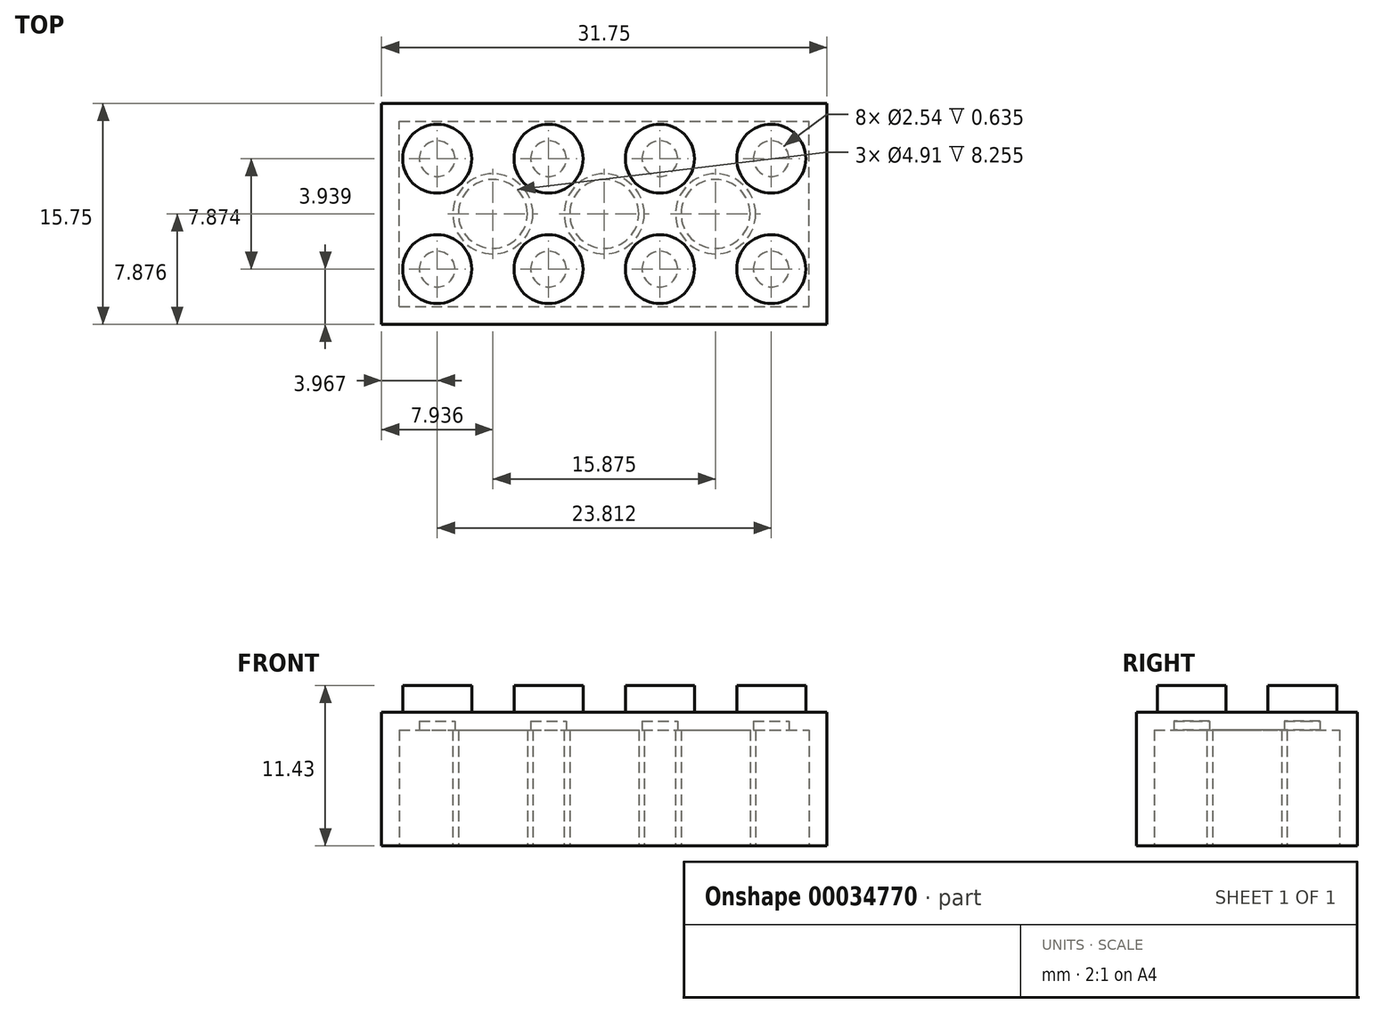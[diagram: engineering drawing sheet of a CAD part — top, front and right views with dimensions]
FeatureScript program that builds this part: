
annotation { "Feature Type Name" : "Feature", "Feature Type Description" : "" }
export const myFeature = defineFeature(function(context is Context, id is Id, definition is map)
    precondition{}
    {
        {
            var Q0;
            Q0=qCreatedBy(makeId("Front.planeOp"),FACE);
            var sketch = newSketch(context, id + "F0", { "sketchPlane" : qUnion([Q0])});
            skLineSegment(sketch, "E0.bottom", {"start": v(-17.81, 25.4) * mm, "end": v(13.94, 25.4) * mm});
            skLineSegment(sketch, "E0.top", {"start": v(-17.81, 13.96) * mm, "end": v(13.94, 13.96) * mm});
            skLineSegment(sketch, "E0.left", {"start": v(-17.81, 25.4) * mm, "end": v(-17.81, 13.96) * mm});
            skLineSegment(sketch, "E0.right", {"start": v(13.94, 25.4) * mm, "end": v(13.94, 13.96) * mm});
            skSolve(sketch);
        }
        {
            var Q0;
            Q0=makeQuery(id+"F0.imprint","IMPRINT",FACE,{"disambiguationData":[TD([[makeQuery(id+"F0.imprint","IMPRINT",EDGE,{"derivedFrom":sQuery(id+"F0.wireOp",EDGE,"E0.bottom")}),-1.0]])]});
            extrude(context, id + "F1", {"entities" : qUnion([Q0]), "depth" : 15.75 * mm});
        }
        {
            var Q0;
            Q0=makeQuery(id+"F1.opExtrude","SWEPT_FACE",FACE,{"disambiguationData":[OSD([sQuery(id+"F0.wireOp",EDGE,"E0.bottom")])]});
            var sketch = newSketch(context, id + "F2", { "sketchPlane" : qUnion([Q0])});
            skCircle(sketch, "E1", {"center": v(9.97, -11.81) * mm, "radius": 2.46 * mm});
            skCircle(sketch, "E2", {"center": v(2.03, -11.81) * mm, "radius": 2.46 * mm});
            skCircle(sketch, "E3", {"center": v(9.97, -3.94) * mm, "radius": 2.46 * mm});
            skCircle(sketch, "E4", {"center": v(2.03, -3.94) * mm, "radius": 2.46 * mm});
            skCircle(sketch, "E5", {"center": v(-5.9, -3.94) * mm, "radius": 2.46 * mm});
            skCircle(sketch, "E6", {"center": v(-5.9, -11.81) * mm, "radius": 2.46 * mm});
            skCircle(sketch, "E7", {"center": v(-13.84, -3.94) * mm, "radius": 2.46 * mm});
            skPoint(sketch, "E7.perimeterSnap0", {"position": v(-13.84, -3.94) * mm});
            skCircle(sketch, "E8", {"center": v(-13.84, -11.81) * mm, "radius": 2.46 * mm});
            skSolve(sketch);
        }
        {
            var Q0;
            Q0=makeQuery(id+"F2.imprint","IMPRINT",FACE,{"disambiguationData":[TD([[makeQuery(id+"F2.imprint","IMPRINT",EDGE,{"derivedFrom":sQuery(id+"F2.wireOp",EDGE,"E1")}),-1.0]])]});
            extrude(context, id + "F3", {"entities" : qUnion([Q0]), "operationType" : NewBodyOperationType.REMOVE, "oppositeDirection" : true, "depth" : 1.9 * mm});
        }
        {
            var Q0;
            Q0=makeQuery(id+"F1.opExtrude","SWEPT_FACE",FACE,{"disambiguationData":[OSD([sQuery(id+"F0.wireOp",EDGE,"E0.top")])]});
            var sketch = newSketch(context, id + "F4", { "sketchPlane" : qUnion([Q0])});
            skCircle(sketch, "E9", {"center": v(-13.84, 11.81) * mm, "radius": 1.27 * mm});
            skCircle(sketch, "E10", {"center": v(-13.84, 3.94) * mm, "radius": 1.27 * mm});
            skCircle(sketch, "E11", {"center": v(-5.9, 3.94) * mm, "radius": 1.27 * mm});
            skCircle(sketch, "E12", {"center": v(2.03, 3.94) * mm, "radius": 1.27 * mm});
            skCircle(sketch, "E13", {"center": v(9.97, 3.94) * mm, "radius": 1.27 * mm});
            skCircle(sketch, "E14", {"center": v(9.97, 11.81) * mm, "radius": 1.27 * mm});
            skCircle(sketch, "E15", {"center": v(2.03, 11.81) * mm, "radius": 1.27 * mm});
            skCircle(sketch, "E16", {"center": v(-5.9, 11.81) * mm, "radius": 1.27 * mm});
            skLineSegment(sketch, "E17.0", {"start": v(-16.54, 1.27) * mm, "end": v(12.67, 1.27) * mm});
            skLineSegment(sketch, "E17.1", {"start": v(-16.54, 14.48) * mm, "end": v(-16.54, 1.27) * mm});
            skLineSegment(sketch, "E17.2", {"start": v(-16.54, 14.48) * mm, "end": v(12.67, 14.48) * mm});
            skLineSegment(sketch, "E17.3", {"start": v(12.67, 14.48) * mm, "end": v(12.67, 1.27) * mm});
            skLineSegment(sketch, "E18", {"start": v(9.97, 3.94) * mm, "end": v(9.97, 11.81) * mm});
            skLineSegment(sketch, "E19", {"start": v(2.03, 11.81) * mm, "end": v(2.03, 3.94) * mm});
            skLineSegment(sketch, "E20", {"start": v(-5.9, 3.94) * mm, "end": v(-5.9, 11.81) * mm});
            skLineSegment(sketch, "E21", {"start": v(-13.84, 11.81) * mm, "end": v(-13.84, 3.94) * mm});
            skLineSegment(sketch, "E22", {"start": v(-13.84, 7.87) * mm, "end": v(-5.9, 7.87) * mm});
            skLineSegment(sketch, "E23", {"start": v(-5.9, 7.87) * mm, "end": v(2.03, 7.87) * mm});
            skLineSegment(sketch, "E24", {"start": v(2.03, 7.87) * mm, "end": v(9.97, 7.87) * mm});
            skCircle(sketch, "E25", {"center": v(6, 7.87) * mm, "radius": 2.86 * mm});
            skCircle(sketch, "E26", {"center": v(-1.94, 7.87) * mm, "radius": 2.86 * mm});
            skCircle(sketch, "E27", {"center": v(-9.87, 7.87) * mm, "radius": 2.86 * mm});
            skCircle(sketch, "E28", {"center": v(6, 7.87) * mm, "radius": 2.46 * mm});
            skCircle(sketch, "E29", {"center": v(-1.94, 7.87) * mm, "radius": 2.46 * mm});
            skCircle(sketch, "E30", {"center": v(-9.87, 7.87) * mm, "radius": 2.46 * mm});
            skSolve(sketch);
        }
        {
            var Q0;
            Q0=makeQuery(id+"F4.imprint","IMPRINT",FACE,{"disambiguationData":[TD([[makeQuery(id+"F4.imprint","IMPRINT",EDGE,{"derivedFrom":sQuery(id+"F4.wireOp",EDGE,"E13")}),1.0]])]});
            var Q1;
            Q1=makeQuery(id+"F4.imprint","IMPRINT",FACE,{"disambiguationData":[TD([[makeQuery(id+"F4.imprint","IMPRINT",EDGE,{"derivedFrom":sQuery(id+"F4.wireOp",EDGE,"E14")}),1.0]])]});
            var Q2;
            Q2=makeQuery(id+"F4.imprint","IMPRINT",FACE,{"disambiguationData":[TD([[makeQuery(id+"F4.imprint","IMPRINT",EDGE,{"derivedFrom":sQuery(id+"F4.wireOp",EDGE,"E15")}),1.0]])]});
            var Q3;
            Q3=makeQuery(id+"F4.imprint","IMPRINT",FACE,{"disambiguationData":[TD([[makeQuery(id+"F4.imprint","IMPRINT",EDGE,{"derivedFrom":sQuery(id+"F4.wireOp",EDGE,"E12")}),1.0]])]});
            var Q4;
            Q4=makeQuery(id+"F4.imprint","IMPRINT",FACE,{"disambiguationData":[TD([[makeQuery(id+"F4.imprint","IMPRINT",EDGE,{"derivedFrom":sQuery(id+"F4.wireOp",EDGE,"E16")}),1.0]])]});
            var Q5;
            Q5=makeQuery(id+"F4.imprint","IMPRINT",FACE,{"disambiguationData":[TD([[makeQuery(id+"F4.imprint","IMPRINT",EDGE,{"derivedFrom":sQuery(id+"F4.wireOp",EDGE,"E11")}),1.0]])]});
            var Q6;
            Q6=makeQuery(id+"F4.imprint","IMPRINT",FACE,{"disambiguationData":[TD([[makeQuery(id+"F4.imprint","IMPRINT",EDGE,{"derivedFrom":sQuery(id+"F4.wireOp",EDGE,"E9")}),1.0]])]});
            var Q7;
            Q7=makeQuery(id+"F4.imprint","IMPRINT",FACE,{"disambiguationData":[TD([[makeQuery(id+"F4.imprint","IMPRINT",EDGE,{"derivedFrom":sQuery(id+"F4.wireOp",EDGE,"E10")}),1.0]])]});
            extrude(context, id + "F5", {"entities" : qUnion([Q0, Q1, Q2, Q3, Q4, Q5, Q6, Q7]), "operationType" : NewBodyOperationType.REMOVE, "oppositeDirection" : true, "depth" : 8.9 * mm});
        }
        {
            var Q0;
            Q0=makeQuery(id+"F4.imprint","IMPRINT",FACE,{"disambiguationData":[TD([[makeQuery(id+"F4.imprint","IMPRINT",EDGE,{"derivedFrom":sQuery(id+"F4.wireOp",EDGE,"E9")}),-1.0]])]});
            var Q1;
            {var subQ0=sQuery(id+"F4.wireOp",EDGE,"E28");var subQ1=sQuery(id+"F4.wireOp",EDGE,"E24");var subQ3=makeQuery(id+"F4.imprint","INTERSECT",VERTEX,{"disambiguationData":[OD(0.0)],"derivedFrom":[subQ1,subQ0]});Q1=makeQuery(id+"F4.imprint","IMPRINT",FACE,{"disambiguationData":[TD([[makeQuery(id+"F4.imprint","IMPRINT",EDGE,{"disambiguationData":[TD([[subQ3,-1.0]])],"derivedFrom":subQ1}),-1.0]])]});}
            var Q2;
            {var subQ0=sQuery(id+"F4.wireOp",EDGE,"E28");var subQ1=sQuery(id+"F4.wireOp",EDGE,"E24");var subQ3=makeQuery(id+"F4.imprint","INTERSECT",VERTEX,{"disambiguationData":[OD(0.0)],"derivedFrom":[subQ1,subQ0]});Q2=makeQuery(id+"F4.imprint","IMPRINT",FACE,{"disambiguationData":[TD([[makeQuery(id+"F4.imprint","IMPRINT",EDGE,{"disambiguationData":[TD([[subQ3,-1.0]])],"derivedFrom":subQ1}),1.0]])]});}
            var Q3;
            {var subQ0=sQuery(id+"F4.wireOp",EDGE,"E29");var subQ1=sQuery(id+"F4.wireOp",EDGE,"E23");var subQ3=makeQuery(id+"F4.imprint","INTERSECT",VERTEX,{"disambiguationData":[OD(0.0)],"derivedFrom":[subQ1,subQ0]});Q3=makeQuery(id+"F4.imprint","IMPRINT",FACE,{"disambiguationData":[TD([[makeQuery(id+"F4.imprint","IMPRINT",EDGE,{"disambiguationData":[TD([[subQ3,-1.0]])],"derivedFrom":subQ1}),-1.0]])]});}
            var Q4;
            {var subQ0=sQuery(id+"F4.wireOp",EDGE,"E29");var subQ1=sQuery(id+"F4.wireOp",EDGE,"E23");var subQ3=makeQuery(id+"F4.imprint","INTERSECT",VERTEX,{"disambiguationData":[OD(0.0)],"derivedFrom":[subQ1,subQ0]});Q4=makeQuery(id+"F4.imprint","IMPRINT",FACE,{"disambiguationData":[TD([[makeQuery(id+"F4.imprint","IMPRINT",EDGE,{"disambiguationData":[TD([[subQ3,-1.0]])],"derivedFrom":subQ1}),1.0]])]});}
            var Q5;
            {var subQ0=sQuery(id+"F4.wireOp",EDGE,"E30");var subQ1=sQuery(id+"F4.wireOp",EDGE,"E22");var subQ3=makeQuery(id+"F4.imprint","INTERSECT",VERTEX,{"disambiguationData":[OD(0.0)],"derivedFrom":[subQ1,subQ0]});Q5=makeQuery(id+"F4.imprint","IMPRINT",FACE,{"disambiguationData":[TD([[makeQuery(id+"F4.imprint","IMPRINT",EDGE,{"disambiguationData":[TD([[subQ3,-1.0]])],"derivedFrom":subQ1}),-1.0]])]});}
            var Q6;
            {var subQ0=sQuery(id+"F4.wireOp",EDGE,"E30");var subQ1=sQuery(id+"F4.wireOp",EDGE,"E22");var subQ3=makeQuery(id+"F4.imprint","INTERSECT",VERTEX,{"disambiguationData":[OD(0.0)],"derivedFrom":[subQ1,subQ0]});Q6=makeQuery(id+"F4.imprint","IMPRINT",FACE,{"disambiguationData":[TD([[makeQuery(id+"F4.imprint","IMPRINT",EDGE,{"disambiguationData":[TD([[subQ3,-1.0]])],"derivedFrom":subQ1}),1.0]])]});}
            extrude(context, id + "F6", {"entities" : qUnion([Q0, Q1, Q2, Q3, Q4, Q5, Q6]), "operationType" : NewBodyOperationType.REMOVE, "oppositeDirection" : true, "depth" : 8.25 * mm});
        }
    });
